# Revit family: Haworth_Swell_StringsThreeLights
name_source: partatom
category: Lighting Fixtures
revit_build: Autodesk Revit 2018 (Build: 20170223_1515(x64)
units: mm (PartAtom-declared; Revit-internal decimal feet)

## family parameters
Always vertical = Yes
Cut with Voids When Loaded = No
Light Source = Yes
OmniClass Number = 23.80.70.11.14
OmniClass Title = General Luminaries, Directional
Part Type = Normal
Room Calculation Point = No
Round Connector Dimension = Use Diameter
Shared = No
Work Plane-Based = No

## types (1)
- LSP4-3610
    Actual Height = 120"
    Assembly Code = D5020200
    Color Filter = 16777215
    Cords Finish = Haworth _ Paint _ Metallic Silver
    Description = Haworth Swell String with Three Lights
    Dimming Lamp Color Temperature Shift = <None>
    Emit Shape Visible in Rendering = No
    Emit from Circle Diameter = 24"
    Glass Finish = Haworth _ Glass _ Clear
    Manufacturer = Haworth
    Model = LSP4-3610
    Photometric Web File = generic
    Revision Number = 1
    Size = Verify Final Dim. w/Haworth
    Tilt Angle = 60.00°
    Top Finish = Haworth _ Metal _ Stainless Steel
    URL = http://www.haworth.com
    URL - Product = https://www.haworth.com
    Warranty = https://www.haworth.com

## geometry (parser evidence)
native form markers: Sweep x6
no freeform markers — native parametric forms only
